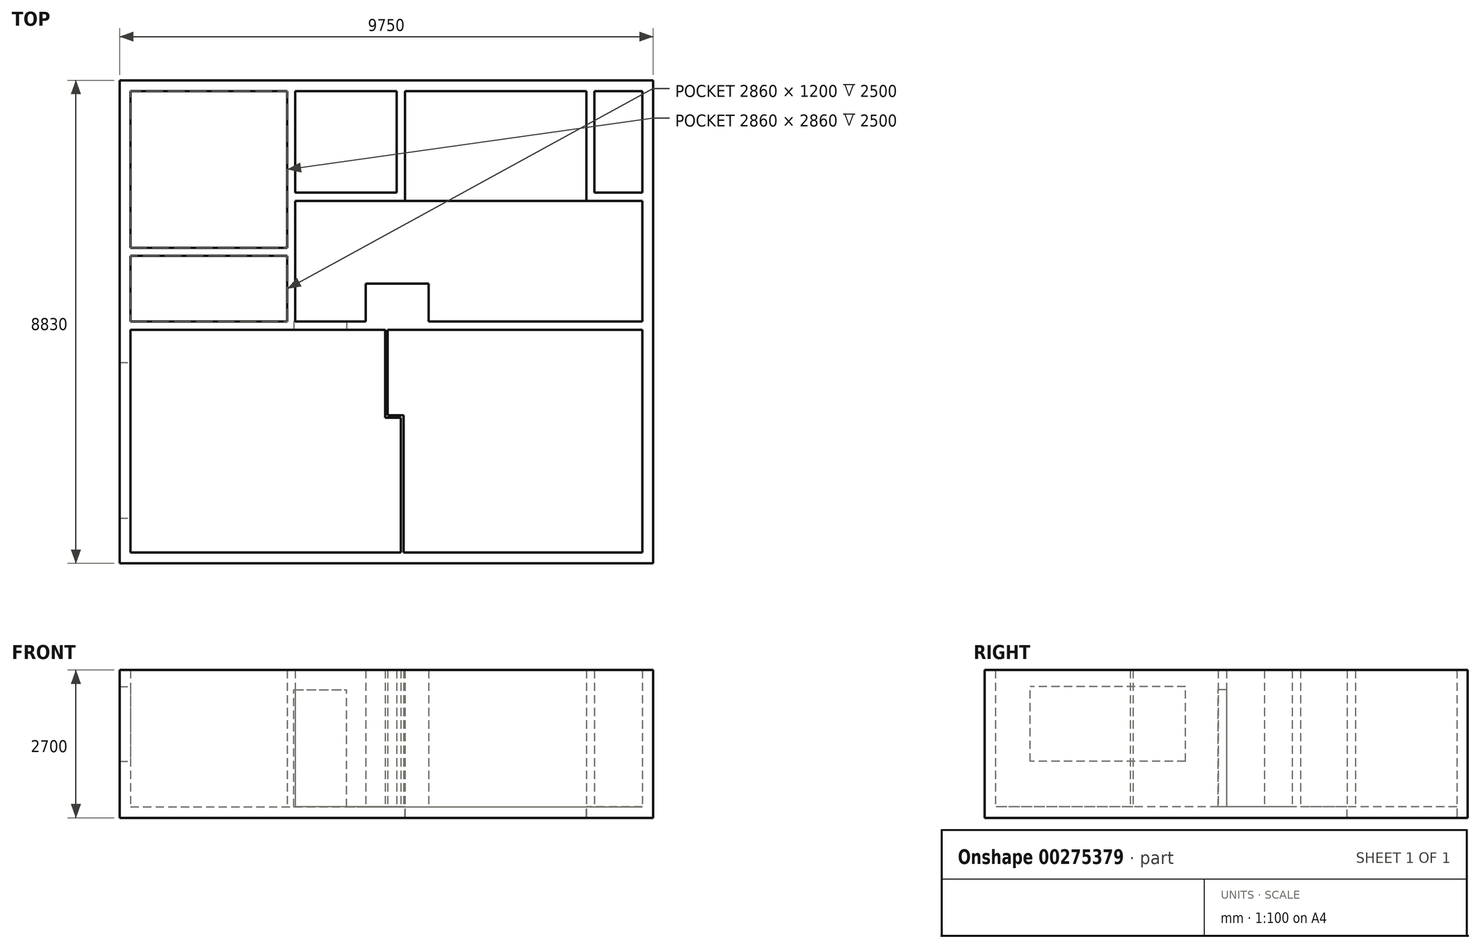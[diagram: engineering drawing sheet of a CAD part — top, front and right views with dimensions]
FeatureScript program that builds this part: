
annotation { "Feature Type Name" : "Feature", "Feature Type Description" : "" }
export const myFeature = defineFeature(function(context is Context, id is Id, definition is map)
    precondition{}
    {
        {
            var Q0;
            Q0=qCreatedBy(makeId("Top.planeOp"),FACE);
            var sketch = newSketch(context, id + "F0", { "sketchPlane" : qUnion([Q0])});
            skLineSegment(sketch, "E0.bottom", {"start": v(0, 0) * mm, "end": v(9750, 0) * mm});
            skLineSegment(sketch, "E0.top", {"start": v(0, -8830) * mm, "end": v(9750, -8830) * mm});
            skLineSegment(sketch, "E0.left", {"start": v(0, 0) * mm, "end": v(0, -8830) * mm});
            skLineSegment(sketch, "E0.right", {"start": v(9750, 0) * mm, "end": v(9750, -8830) * mm});
            skLineSegment(sketch, "E1.bottom", {"start": v(200, -200) * mm, "end": v(3060, -200) * mm});
            skLineSegment(sketch, "E1.top", {"start": v(200, -3060) * mm, "end": v(3060, -3060) * mm});
            skLineSegment(sketch, "E1.left", {"start": v(200, -200) * mm, "end": v(200, -3060) * mm});
            skLineSegment(sketch, "E2", {"start": v(3060, -200) * mm, "end": v(3060, -1450) * mm});
            skLineSegment(sketch, "E3", {"start": v(3060, -1450) * mm, "end": v(3060, -1450) * mm});
            skLineSegment(sketch, "E4", {"start": v(3060, -1450) * mm, "end": v(3060, -3060) * mm});
            skLineSegment(sketch, "E5", {"start": v(3210, -200) * mm, "end": v(3210, -1300) * mm});
            skLineSegment(sketch, "E6", {"start": v(3210, -1300) * mm, "end": v(3210, -1300) * mm});
            skLineSegment(sketch, "E7", {"start": v(3210, -1300) * mm, "end": v(3210, -2055) * mm});
            skLineSegment(sketch, "E8", {"start": v(3210, -2055) * mm, "end": v(5065, -2055) * mm});
            skLineSegment(sketch, "E9", {"start": v(5065, -2055) * mm, "end": v(5065, -200) * mm});
            skLineSegment(sketch, "E10", {"start": v(5065, -200) * mm, "end": v(3210, -200) * mm});
            skLineSegment(sketch, "E11.bottom", {"start": v(200, -4560) * mm, "end": v(4850, -4560) * mm});
            skLineSegment(sketch, "E11.top", {"start": v(200, -8630) * mm, "end": v(5140, -8630) * mm});
            skLineSegment(sketch, "E11.left", {"start": v(200, -4560) * mm, "end": v(200, -8630) * mm});
            skLineSegment(sketch, "E12.bottom", {"start": v(4900, -4560) * mm, "end": v(9550, -4560) * mm});
            skLineSegment(sketch, "E12.top", {"start": v(5190, -8630) * mm, "end": v(9550, -8630) * mm});
            skLineSegment(sketch, "E12.right", {"start": v(9550, -4560) * mm, "end": v(9550, -8630) * mm});
            skLineSegment(sketch, "E13", {"start": v(3210, -2205) * mm, "end": v(3210, -4410) * mm});
            skLineSegment(sketch, "E14", {"start": v(3210, -4410) * mm, "end": v(4495.23, -4410) * mm});
            skLineSegment(sketch, "E15", {"start": v(4495.23, -4410) * mm, "end": v(4495.23, -3719.03) * mm});
            skLineSegment(sketch, "E16", {"start": v(4495.23, -3719.03) * mm, "end": v(5645.15, -3719.03) * mm});
            skLineSegment(sketch, "E17", {"start": v(5645.15, -3719.03) * mm, "end": v(5645.15, -4410) * mm});
            skLineSegment(sketch, "E18", {"start": v(5645.15, -4410) * mm, "end": v(9550, -4410) * mm});
            skLineSegment(sketch, "E19", {"start": v(9550, -4410) * mm, "end": v(9550, -2205) * mm});
            skLineSegment(sketch, "E20", {"start": v(9550, -2205) * mm, "end": v(8528.75, -2205) * mm});
            skLineSegment(sketch, "E21", {"start": v(8528.75, -2205) * mm, "end": v(8528.75, -200) * mm});
            skLineSegment(sketch, "E22", {"start": v(8528.75, -200) * mm, "end": v(5215, -200) * mm});
            skLineSegment(sketch, "E23", {"start": v(5215, -200) * mm, "end": v(5215, -2205) * mm});
            skLineSegment(sketch, "E24", {"start": v(5215, -2205) * mm, "end": v(3210, -2205) * mm});
            skLineSegment(sketch, "E25.bottom", {"start": v(8678.75, -200) * mm, "end": v(9550, -200) * mm});
            skLineSegment(sketch, "E25.top", {"start": v(8678.75, -2055) * mm, "end": v(9550, -2055) * mm});
            skLineSegment(sketch, "E25.left", {"start": v(8678.75, -200) * mm, "end": v(8678.75, -2055) * mm});
            skLineSegment(sketch, "E25.right", {"start": v(9550, -200) * mm, "end": v(9550, -2055) * mm});
            skLineSegment(sketch, "E26.bottom", {"start": v(200, -3210) * mm, "end": v(3060, -3210) * mm});
            skLineSegment(sketch, "E26.top", {"start": v(200, -4410) * mm, "end": v(3060, -4410) * mm});
            skLineSegment(sketch, "E26.left", {"start": v(200, -3210) * mm, "end": v(200, -4410) * mm});
            skLineSegment(sketch, "E26.right", {"start": v(3060, -3210) * mm, "end": v(3060, -4410) * mm});
            skLineSegment(sketch, "E27", {"start": v(4850, -4560) * mm, "end": v(4850, -6170) * mm});
            skLineSegment(sketch, "E28", {"start": v(4850, -6170) * mm, "end": v(5140, -6170) * mm});
            skLineSegment(sketch, "E29", {"start": v(5140, -6170) * mm, "end": v(5140, -8630) * mm});
            skLineSegment(sketch, "E30.0", {"start": v(5190, -6120) * mm, "end": v(5190, -8630) * mm});
            skLineSegment(sketch, "E30.1", {"start": v(4900, -6120) * mm, "end": v(5190, -6120) * mm});
            skLineSegment(sketch, "E30.2", {"start": v(4900, -4560) * mm, "end": v(4900, -6120) * mm});
            skSolve(sketch);
        }
        {
            var Q0;
            Q0 = qSketchRegion(id + "F0", true);
            extrude(context, id + "F1", {"entities" : qUnion([Q0]), "depth" : 2500 * mm});
        }
        {
            var Q0;
            Q0=makeQuery(id+"F1.opExtrude","CAP_FACE",FACE,{"disambiguationData":[OSD([sQuery(id+"F0.wireOp",EDGE,"E0.bottom"),sQuery(id+"F0.wireOp",EDGE,"E0.top"),sQuery(id+"F0.wireOp",EDGE,"E0.left"),sQuery(id+"F0.wireOp",EDGE,"E0.right"),sQuery(id+"F0.wireOp",EDGE,"E1.bottom"),sQuery(id+"F0.wireOp",EDGE,"E1.top"),sQuery(id+"F0.wireOp",EDGE,"E1.left"),sQuery(id+"F0.wireOp",EDGE,"E2"),sQuery(id+"F0.wireOp",EDGE,"E3"),sQuery(id+"F0.wireOp",EDGE,"E4"),sQuery(id+"F0.wireOp",EDGE,"E5"),sQuery(id+"F0.wireOp",EDGE,"E6"),sQuery(id+"F0.wireOp",EDGE,"E7"),sQuery(id+"F0.wireOp",EDGE,"E8"),sQuery(id+"F0.wireOp",EDGE,"E9"),sQuery(id+"F0.wireOp",EDGE,"E10"),sQuery(id+"F0.wireOp",EDGE,"E11.bottom"),sQuery(id+"F0.wireOp",EDGE,"E11.top"),sQuery(id+"F0.wireOp",EDGE,"E11.left"),sQuery(id+"F0.wireOp",EDGE,"E11.right"),sQuery(id+"F0.wireOp",EDGE,"E12.bottom"),sQuery(id+"F0.wireOp",EDGE,"E12.top"),sQuery(id+"F0.wireOp",EDGE,"E12.left"),sQuery(id+"F0.wireOp",EDGE,"E12.right"),sQuery(id+"F0.wireOp",EDGE,"E13"),sQuery(id+"F0.wireOp",EDGE,"E14"),sQuery(id+"F0.wireOp",EDGE,"E15"),sQuery(id+"F0.wireOp",EDGE,"E16"),sQuery(id+"F0.wireOp",EDGE,"E17"),sQuery(id+"F0.wireOp",EDGE,"E18"),sQuery(id+"F0.wireOp",EDGE,"E19"),sQuery(id+"F0.wireOp",EDGE,"E20"),sQuery(id+"F0.wireOp",EDGE,"E21"),sQuery(id+"F0.wireOp",EDGE,"E22"),sQuery(id+"F0.wireOp",EDGE,"E23"),sQuery(id+"F0.wireOp",EDGE,"E24"),sQuery(id+"F0.wireOp",EDGE,"E25.bottom"),sQuery(id+"F0.wireOp",EDGE,"E25.top"),sQuery(id+"F0.wireOp",EDGE,"E25.left"),sQuery(id+"F0.wireOp",EDGE,"E25.right")])],"isStart":true});
            var sketch = newSketch(context, id + "F2", { "sketchPlane" : qUnion([Q0])});
            skLineSegment(sketch, "E31.bottom", {"start": v(9750, 8830) * mm, "end": v(0, 8830) * mm});
            skLineSegment(sketch, "E31.top", {"start": v(9750, 0) * mm, "end": v(0, 0) * mm});
            skLineSegment(sketch, "E31.left", {"start": v(9750, 8830) * mm, "end": v(9750, 0) * mm});
            skLineSegment(sketch, "E31.right", {"start": v(0, 8830) * mm, "end": v(0, 0) * mm});
            skLineSegment(sketch, "E32.bottom", {"start": v(5215, 200) * mm, "end": v(8528.75, 200) * mm});
            skLineSegment(sketch, "E32.top", {"start": v(5215, 2205) * mm, "end": v(8528.75, 2205) * mm});
            skLineSegment(sketch, "E32.left", {"start": v(5215, 200) * mm, "end": v(5215, 2205) * mm});
            skLineSegment(sketch, "E32.right", {"start": v(8528.75, 200) * mm, "end": v(8528.75, 2205) * mm});
            skSolve(sketch);
        }
        {
            var Q0;
            Q0 = qSketchRegion(id + "F2", true);
            extrude(context, id + "F3", {"entities" : qUnion([Q0]), "operationType" : NewBodyOperationType.ADD, "depth" : 200 * mm});
        }
        {
            var Q0;
            Q0=makeQuery(id+"F1.opExtrude","SWEPT_FACE",FACE,{"disambiguationData":[OSD([sQuery(id+"F0.wireOp",EDGE,"E11.bottom")])]});
            var sketch = newSketch(context, id + "F4", { "sketchPlane" : qUnion([Q0])});
            skLineSegment(sketch, "E33.bottom", {"start": v(3185, 0) * mm, "end": v(4150, 0) * mm});
            skLineSegment(sketch, "E33.top", {"start": v(3185, 2140) * mm, "end": v(4150, 2140) * mm});
            skLineSegment(sketch, "E33.left", {"start": v(3185, 0) * mm, "end": v(3185, 2140) * mm});
            skLineSegment(sketch, "E33.right", {"start": v(4150, 0) * mm, "end": v(4150, 2140) * mm});
            skSolve(sketch);
        }
        {
            var Q0;
            Q0 = qSketchRegion(id + "F4", true);
            var Q1;
            Q1=makeQuery(id+"F1.opExtrude","SWEPT_FACE",FACE,{"disambiguationData":[OSD([sQuery(id+"F0.wireOp",EDGE,"E14")])]});
            extrude(context, id + "F5", {"entities" : qUnion([Q0]), "operationType" : NewBodyOperationType.REMOVE, "endBound" : BoundingType.UP_TO_SURFACE, "oppositeDirection" : true, "endBoundEntityFace" : qUnion([Q1]), "depth" : 25 * mm});
        }
        {
            var Q0;
            Q0=makeQuery(id+"F1.opExtrude","SWEPT_FACE",FACE,{"disambiguationData":[OSD([sQuery(id+"F0.wireOp",EDGE,"E11.left")])]});
            var sketch = newSketch(context, id + "F6", { "sketchPlane" : qUnion([Q0])});
            skLineSegment(sketch, "E34.bottom", {"start": v(-8000, 2200) * mm, "end": v(-5160, 2200) * mm});
            skLineSegment(sketch, "E34.top", {"start": v(-8000, 830) * mm, "end": v(-5160, 830) * mm});
            skLineSegment(sketch, "E34.left", {"start": v(-8000, 2200) * mm, "end": v(-8000, 830) * mm});
            skLineSegment(sketch, "E34.right", {"start": v(-5160, 2200) * mm, "end": v(-5160, 830) * mm});
            skSolve(sketch);
        }
        {
            var Q0;
            Q0 = qSketchRegion(id + "F6", true);
            var Q1;
            Q1=makeQuery(id+"F3.boolean.opBoolean","MERGE",FACE,{"derivedFrom":[makeQuery(id+"F1.opExtrude","SWEPT_FACE",FACE,{"disambiguationData":[OSD([sQuery(id+"F0.wireOp",EDGE,"E0.left")])]}),makeQuery(id+"F3.opExtrude","SWEPT_FACE",FACE,{"disambiguationData":[OSD([sQuery(id+"F2.wireOp",EDGE,"E31.right")])]})]});
            extrude(context, id + "F7", {"entities" : qUnion([Q0]), "operationType" : NewBodyOperationType.REMOVE, "endBound" : BoundingType.UP_TO_SURFACE, "oppositeDirection" : true, "endBoundEntityFace" : qUnion([Q1]), "depth" : 25 * mm});
        }
    });
